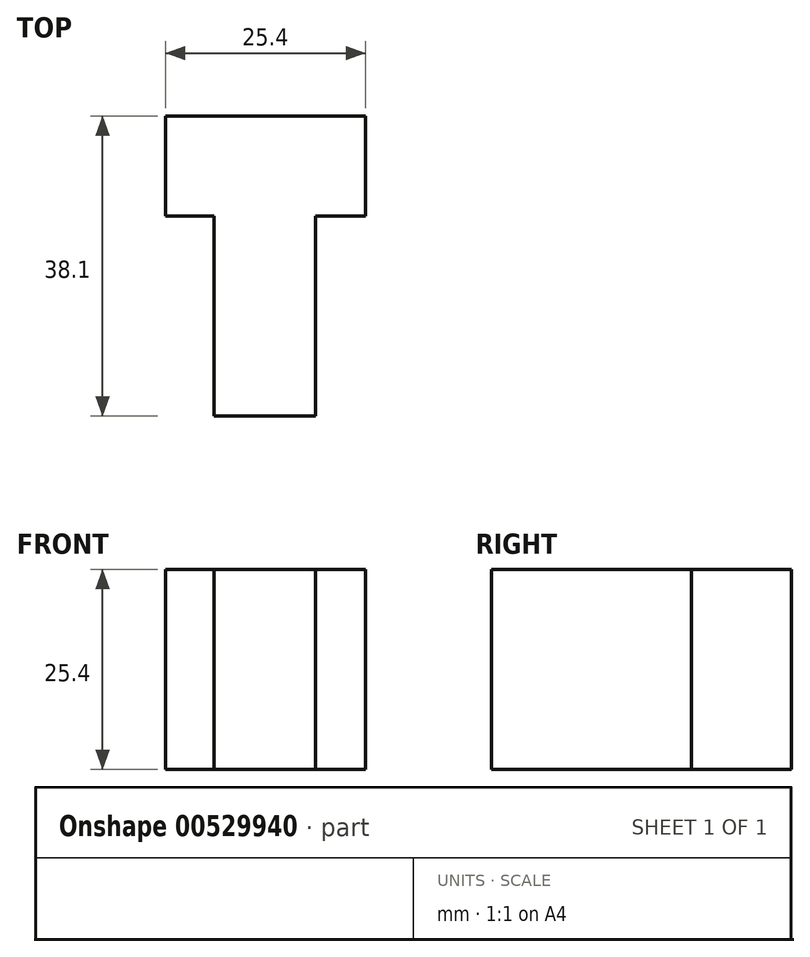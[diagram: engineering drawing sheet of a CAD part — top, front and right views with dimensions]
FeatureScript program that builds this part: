
annotation { "Feature Type Name" : "Feature", "Feature Type Description" : "" }
export const myFeature = defineFeature(function(context is Context, id is Id, definition is map)
    precondition{}
    {
        {
            var Q0;
            Q0=qCreatedBy(makeId("Top.planeOp"),FACE);
            var sketch = newSketch(context, id + "F0", { "sketchPlane" : qUnion([Q0])});
            skLineSegment(sketch, "E0", {"start": v(-52.1, 49.7) * mm, "end": v(-52.1, 37) * mm});
            skLineSegment(sketch, "E1", {"start": v(-52.1, 49.7) * mm, "end": v(-26.7, 49.7) * mm});
            skLineSegment(sketch, "E2", {"start": v(-26.7, 49.7) * mm, "end": v(-26.7, 37) * mm});
            skLineSegment(sketch, "E3", {"start": v(-52.1, 37) * mm, "end": v(-45.97, 37) * mm});
            skLineSegment(sketch, "E4", {"start": v(-26.7, 37) * mm, "end": v(-33.06, 37) * mm});
            skLineSegment(sketch, "E5", {"start": v(-45.97, 37) * mm, "end": v(-45.97, 11.6) * mm});
            skLineSegment(sketch, "E6", {"start": v(-33.06, 37) * mm, "end": v(-33.06, 11.6) * mm});
            skLineSegment(sketch, "E7", {"start": v(-45.97, 11.6) * mm, "end": v(-33.06, 11.6) * mm});
            skSolve(sketch);
        }
        {
            var Q0;
            Q0 = qSketchRegion(id + "F0", true);
            extrude(context, id + "F1", {"entities" : qUnion([Q0]), "depth" : 25.4 * mm, "offsetDistance" : 25.4 * mm});
        }
    });
